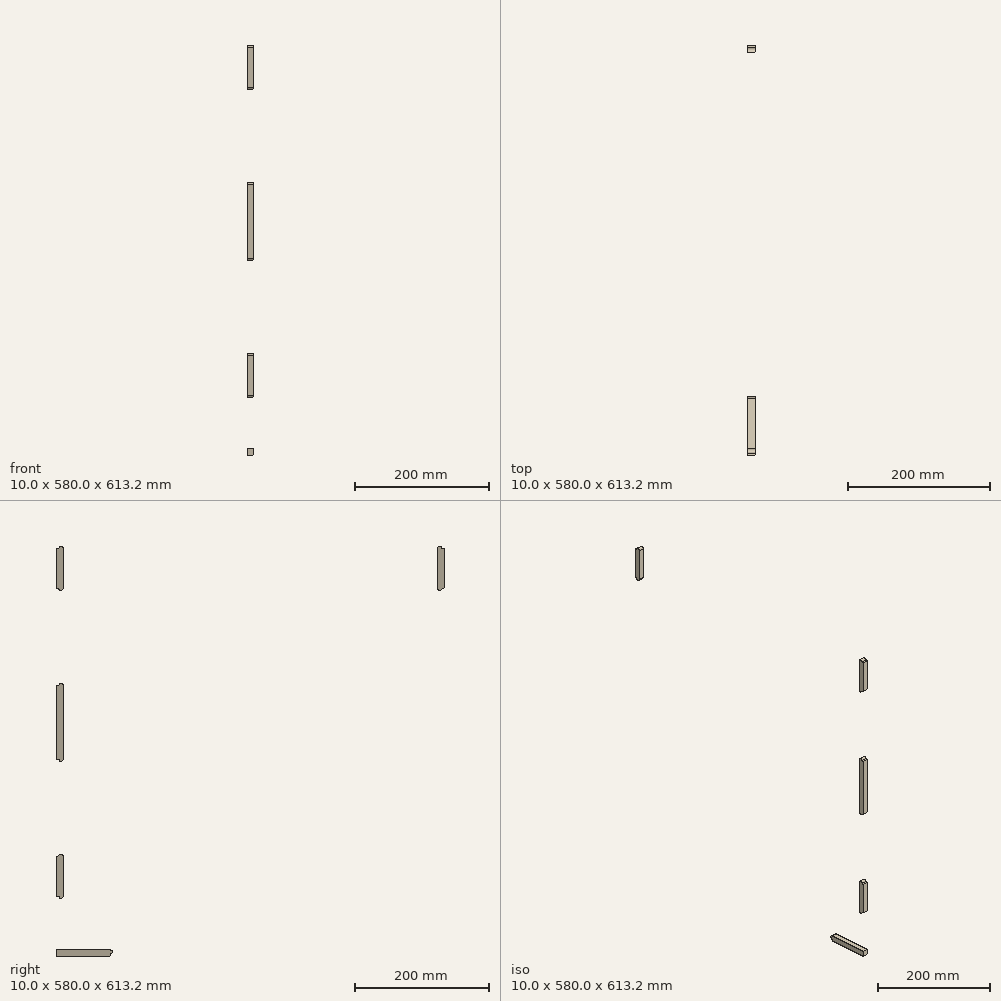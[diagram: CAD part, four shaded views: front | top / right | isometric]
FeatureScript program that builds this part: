
annotation { "Feature Type Name" : "Feature", "Feature Type Description" : "" }
export const myFeature = defineFeature(function(context is Context, id is Id, definition is map)
    precondition{}
    {
        {
            var Q0;
            Q0=qCreatedBy(makeId("Right.planeOp"),FACE);
            var sketch = newSketch(context, id + "F0", { "sketchPlane" : qUnion([Q0])});
            skLineSegment(sketch, "E0.bottom", {"start": v(290, -350) * mm, "end": v(-290, -350) * mm});
            skLineSegment(sketch, "E0.top", {"start": v(290, 350) * mm, "end": v(-290, 350) * mm});
            skLineSegment(sketch, "E0.left", {"start": v(290, -350) * mm, "end": v(290, 350) * mm});
            skLineSegment(sketch, "E0.right", {"start": v(-290, -350) * mm, "end": v(-290, 350) * mm});
            skPoint(sketch, "E0.middle", {"position": v(0, 0) * mm});
            skSolve(sketch);
        }
        {
            var Q0;
            Q0 = qSketchRegion(id + "F0", true);
            extrude(context, id + "F1", {"entities" : qUnion([Q0]), "depth" : 10 * mm, "offsetDistance" : 25 * mm});
        }
        {
            var Q0;
            Q0=makeQuery(id+"F1.opExtrude","CAP_FACE",FACE,{"disambiguationData":[OSD([sQuery(id+"F0.wireOp",EDGE,"E0.bottom"),sQuery(id+"F0.wireOp",EDGE,"E0.top"),sQuery(id+"F0.wireOp",EDGE,"E0.left"),sQuery(id+"F0.wireOp",EDGE,"E0.right")])],"isStart":false});
            var sketch = newSketch(context, id + "F2", { "sketchPlane" : qUnion([Q0])});
            skLineSegment(sketch, "E1", {"start": v(0, 350) * mm, "end": v(0, -350) * mm, "construction": true});
            skLineSegment(sketch, "E2", {"start": v(-281.72, 0) * mm, "end": v(290, 0) * mm, "construction": true});
            skLineSegment(sketch, "E3", {"start": v(150, -346.5) * mm, "end": v(150, -350) * mm});
            skLineSegment(sketch, "E4", {"start": v(210, -350) * mm, "end": v(210, -346.5) * mm});
            skLineSegment(sketch, "E5", {"start": v(210, -340) * mm, "end": v(290, -340) * mm});
            skLineSegment(sketch, "E6", {"start": v(290, -340) * mm, "end": v(290, -260) * mm});
            skLineSegment(sketch, "E7", {"start": v(290, -260) * mm, "end": v(286.5, -260) * mm});
            skLineSegment(sketch, "E8", {"start": v(280, -260) * mm, "end": v(280, -200) * mm});
            skLineSegment(sketch, "E9", {"start": v(286.5, -200) * mm, "end": v(290, -200) * mm});
            skLineSegment(sketch, "E10", {"start": v(290, -200) * mm, "end": v(290, -55) * mm});
            skLineSegment(sketch, "E11", {"start": v(290, -55) * mm, "end": v(286.5, -55) * mm});
            skLineSegment(sketch, "E12", {"start": v(280, -55) * mm, "end": v(280, 0) * mm});
            skArc(sketch, "E13", {"start": v(150, -346.5) * mm, "mid": v(153.25, -343.25) * mm, "end": v(150, -340) * mm});
            skArc(sketch, "E14", {"start": v(210, -340) * mm, "mid": v(206.75, -343.25) * mm, "end": v(210, -346.5) * mm});
            skArc(sketch, "E15", {"start": v(280, -55) * mm, "mid": v(283.25, -58.25) * mm, "end": v(286.5, -55) * mm});
            skArc(sketch, "E16", {"start": v(280, -260) * mm, "mid": v(283.25, -263.25) * mm, "end": v(286.5, -260) * mm});
            skArc(sketch, "E17", {"start": v(286.5, -200) * mm, "mid": v(283.25, -196.75) * mm, "end": v(280, -200) * mm});
            skLineSegment(sketch, "E18", {"start": v(150, -340) * mm, "end": v(55, -340) * mm});
            skLineSegment(sketch, "E19", {"start": v(210, -350) * mm, "end": v(150, -350) * mm});
            skLineSegment(sketch, "E20", {"start": v(55, -346.5) * mm, "end": v(55, -350) * mm});
            skLineSegment(sketch, "E21", {"start": v(55, -350) * mm, "end": v(0, -350) * mm});
            skArc(sketch, "E22", {"start": v(55, -340) * mm, "mid": v(51.75, -343.25) * mm, "end": v(55, -346.5) * mm});
            skLineSegment(sketch, "E23.MirrorCS", {"start": v(-150, -346.5) * mm, "end": v(-150, -350) * mm});
            skLineSegment(sketch, "E24.MirrorCS", {"start": v(-290, -260) * mm, "end": v(-286.5, -260) * mm});
            skArc(sketch, "E25.MirrorCS", {"start": v(-150, -346.5) * mm, "mid": v(-153.25, -343.25) * mm, "end": v(-150, -340) * mm});
            skLineSegment(sketch, "E26.MirrorCS", {"start": v(-290, -55) * mm, "end": v(-286.5, -55) * mm});
            skArc(sketch, "E27.MirrorCS", {"start": v(-280, -55) * mm, "mid": v(-283.25, -58.25) * mm, "end": v(-286.5, -55) * mm});
            skArc(sketch, "E28.MirrorCS", {"start": v(-280, -260) * mm, "mid": v(-283.25, -263.25) * mm, "end": v(-286.5, -260) * mm});
            skArc(sketch, "E29.MirrorCS", {"start": v(-55, -340) * mm, "mid": v(-51.75, -343.25) * mm, "end": v(-55, -346.5) * mm});
            skArc(sketch, "E30.MirrorCS", {"start": v(-210, -340) * mm, "mid": v(-206.75, -343.25) * mm, "end": v(-210, -346.5) * mm});
            skLineSegment(sketch, "E31.MirrorCS", {"start": v(-55, -346.5) * mm, "end": v(-55, -350) * mm});
            skArc(sketch, "E32.MirrorCS", {"start": v(-286.5, -200) * mm, "mid": v(-283.25, -196.75) * mm, "end": v(-280, -200) * mm});
            skLineSegment(sketch, "E33.MirrorCS", {"start": v(-286.5, -200) * mm, "end": v(-290, -200) * mm});
            skLineSegment(sketch, "E34.MirrorCS", {"start": v(-210, -350) * mm, "end": v(-210, -346.5) * mm});
            skLineSegment(sketch, "E35.MirrorCS", {"start": v(-55, -350) * mm, "end": v(0, -350) * mm});
            skLineSegment(sketch, "E36.MirrorCS", {"start": v(-210, -340) * mm, "end": v(-290, -340) * mm});
            skLineSegment(sketch, "E37.MirrorCS", {"start": v(-290, -340) * mm, "end": v(-290, -260) * mm});
            skLineSegment(sketch, "E38.MirrorCS", {"start": v(-210, -350) * mm, "end": v(-150, -350) * mm});
            skLineSegment(sketch, "E39.MirrorCS", {"start": v(-280, -55) * mm, "end": v(-280, 0) * mm});
            skLineSegment(sketch, "E40.MirrorCS", {"start": v(-280, -260) * mm, "end": v(-280, -200) * mm});
            skLineSegment(sketch, "E41.MirrorCS", {"start": v(-150, -340) * mm, "end": v(-55, -340) * mm});
            skLineSegment(sketch, "E42.MirrorCS", {"start": v(-290, -200) * mm, "end": v(-290, -55) * mm});
            skLineSegment(sketch, "E43.MirrorCS", {"start": v(281.72, 0) * mm, "end": v(-290, 0) * mm, "construction": true});
            skLineSegment(sketch, "E44.MirrorCS", {"start": v(55, 346.5) * mm, "end": v(55, 350) * mm});
            skArc(sketch, "E45.MirrorCS", {"start": v(55, 340) * mm, "mid": v(51.75, 343.25) * mm, "end": v(55, 346.5) * mm});
            skArc(sketch, "E46.MirrorCS", {"start": v(280, 260) * mm, "mid": v(283.25, 263.25) * mm, "end": v(286.5, 260) * mm});
            skArc(sketch, "E47.MirrorCS", {"start": v(-150, 346.5) * mm, "mid": v(-153.25, 343.25) * mm, "end": v(-150, 340) * mm});
            skArc(sketch, "E48.MirrorCS", {"start": v(280, 55) * mm, "mid": v(283.25, 58.25) * mm, "end": v(286.5, 55) * mm});
            skLineSegment(sketch, "E49.MirrorCS", {"start": v(210, 350) * mm, "end": v(210, 346.5) * mm});
            skLineSegment(sketch, "E50.MirrorCS", {"start": v(-290, 260) * mm, "end": v(-286.5, 260) * mm});
            skLineSegment(sketch, "E51.MirrorCS", {"start": v(290, 260) * mm, "end": v(286.5, 260) * mm});
            skArc(sketch, "E52.MirrorCS", {"start": v(210, 340) * mm, "mid": v(206.75, 343.25) * mm, "end": v(210, 346.5) * mm});
            skLineSegment(sketch, "E53.MirrorCS", {"start": v(286.5, 200) * mm, "end": v(290, 200) * mm});
            skArc(sketch, "E54.MirrorCS", {"start": v(-280, 260) * mm, "mid": v(-283.25, 263.25) * mm, "end": v(-286.5, 260) * mm});
            skLineSegment(sketch, "E55.MirrorCS", {"start": v(-150, 346.5) * mm, "end": v(-150, 350) * mm});
            skLineSegment(sketch, "E56.MirrorCS", {"start": v(290, 55) * mm, "end": v(286.5, 55) * mm});
            skArc(sketch, "E57.MirrorCS", {"start": v(-210, 340) * mm, "mid": v(-206.75, 343.25) * mm, "end": v(-210, 346.5) * mm});
            skLineSegment(sketch, "E58.MirrorCS", {"start": v(150, 346.5) * mm, "end": v(150, 350) * mm});
            skLineSegment(sketch, "E59.MirrorCS", {"start": v(-286.5, 200) * mm, "end": v(-290, 200) * mm});
            skArc(sketch, "E60.MirrorCS", {"start": v(286.5, 200) * mm, "mid": v(283.25, 196.75) * mm, "end": v(280, 200) * mm});
            skArc(sketch, "E61.MirrorCS", {"start": v(150, 346.5) * mm, "mid": v(153.25, 343.25) * mm, "end": v(150, 340) * mm});
            skLineSegment(sketch, "E62.MirrorCS", {"start": v(-210, 350) * mm, "end": v(-210, 346.5) * mm});
            skArc(sketch, "E63.MirrorCS", {"start": v(-286.5, 200) * mm, "mid": v(-283.25, 196.75) * mm, "end": v(-280, 200) * mm});
            skLineSegment(sketch, "E64.MirrorCS", {"start": v(-55, 346.5) * mm, "end": v(-55, 350) * mm});
            skArc(sketch, "E65.MirrorCS", {"start": v(-55, 340) * mm, "mid": v(-51.75, 343.25) * mm, "end": v(-55, 346.5) * mm});
            skLineSegment(sketch, "E66.MirrorCS", {"start": v(-290, 55) * mm, "end": v(-286.5, 55) * mm});
            skLineSegment(sketch, "E67.MirrorCS", {"start": v(55, 350) * mm, "end": v(0, 350) * mm});
            skArc(sketch, "E68.MirrorCS", {"start": v(-280, 55) * mm, "mid": v(-283.25, 58.25) * mm, "end": v(-286.5, 55) * mm});
            skLineSegment(sketch, "E69.MirrorCS", {"start": v(280, 260) * mm, "end": v(280, 200) * mm});
            skLineSegment(sketch, "E70.MirrorCS", {"start": v(150, 340) * mm, "end": v(55, 340) * mm});
            skLineSegment(sketch, "E71.MirrorCS", {"start": v(210, 340) * mm, "end": v(290, 340) * mm});
            skLineSegment(sketch, "E72.MirrorCS", {"start": v(290, 340) * mm, "end": v(290, 260) * mm});
            skLineSegment(sketch, "E73.MirrorCS", {"start": v(280, 55) * mm, "end": v(280, 0) * mm});
            skLineSegment(sketch, "E74.MirrorCS", {"start": v(-280, 55) * mm, "end": v(-280, 0) * mm});
            skLineSegment(sketch, "E75.MirrorCS", {"start": v(210, 350) * mm, "end": v(150, 350) * mm});
            skLineSegment(sketch, "E76.MirrorCS", {"start": v(-280, 260) * mm, "end": v(-280, 200) * mm});
            skLineSegment(sketch, "E77.MirrorCS", {"start": v(290, 200) * mm, "end": v(290, 55) * mm});
            skLineSegment(sketch, "E78.MirrorCS", {"start": v(-55, 350) * mm, "end": v(0, 350) * mm});
            skLineSegment(sketch, "E79.MirrorCS", {"start": v(-290, 200) * mm, "end": v(-290, 55) * mm});
            skLineSegment(sketch, "E80.MirrorCS", {"start": v(-150, 340) * mm, "end": v(-55, 340) * mm});
            skLineSegment(sketch, "E81.MirrorCS", {"start": v(-210, 350) * mm, "end": v(-150, 350) * mm});
            skLineSegment(sketch, "E82.MirrorCS", {"start": v(-210, 340) * mm, "end": v(-290, 340) * mm});
            skLineSegment(sketch, "E83.MirrorCS", {"start": v(-290, 340) * mm, "end": v(-290, 260) * mm});
            skSolve(sketch);
        }
        {
            var Q0;
            Q0=makeQuery(id+"F2.imprint","IMPRINT",FACE,{"disambiguationData":[TD([[makeQuery(id+"F2.imprint","IMPRINT",EDGE,{"derivedFrom":sQuery(id+"F2.wireOp",EDGE,"E30.MirrorCS")}),-1.0]])]});
            var Q1;
            {var subQ1=sQuery(id+"F2.wireOp",EDGE,"E23.MirrorCS");Q1=makeQuery(id+"F2.imprint","IMPRINT",FACE,{"disambiguationData":[TD([[makeQuery(id+"F2.imprint","IMPRINT",EDGE,{"derivedFrom":subQ1}),1.0]])]});}
            var Q2;
            {var subQ1=sQuery(id+"F2.wireOp",EDGE,"E3");Q2=makeQuery(id+"F2.imprint","IMPRINT",FACE,{"disambiguationData":[TD([[makeQuery(id+"F2.imprint","IMPRINT",EDGE,{"derivedFrom":subQ1}),-1.0]])]});}
            var Q3;
            {var subQ3=sQuery(id+"F2.wireOp",EDGE,"E4");Q3=makeQuery(id+"F2.imprint","IMPRINT",FACE,{"disambiguationData":[TD([[makeQuery(id+"F2.imprint","IMPRINT",EDGE,{"derivedFrom":subQ3}),-1.0]])]});}
            var Q4;
            {var subQ0=sQuery(id+"F2.wireOp",EDGE,"E7");Q4=makeQuery(id+"F2.imprint","IMPRINT",FACE,{"disambiguationData":[TD([[makeQuery(id+"F2.imprint","IMPRINT",EDGE,{"derivedFrom":subQ0}),-1.0]])]});}
            var Q5;
            {var subQ0=sQuery(id+"F2.wireOp",EDGE,"E11");Q5=makeQuery(id+"F2.imprint","IMPRINT",FACE,{"disambiguationData":[TD([[makeQuery(id+"F2.imprint","IMPRINT",EDGE,{"derivedFrom":subQ0}),-1.0]])]});}
            var Q6;
            Q6=makeQuery(id+"F2.imprint","IMPRINT",FACE,{"disambiguationData":[TD([[makeQuery(id+"F2.imprint","IMPRINT",EDGE,{"derivedFrom":sQuery(id+"F2.wireOp",EDGE,"E46.MirrorCS")}),-1.0]])]});
            var Q7;
            {var subQ3=sQuery(id+"F2.wireOp",EDGE,"E49.MirrorCS");Q7=makeQuery(id+"F2.imprint","IMPRINT",FACE,{"disambiguationData":[TD([[makeQuery(id+"F2.imprint","IMPRINT",EDGE,{"derivedFrom":subQ3}),1.0]])]});}
            var Q8;
            {var subQ1=sQuery(id+"F2.wireOp",EDGE,"E44.MirrorCS");Q8=makeQuery(id+"F2.imprint","IMPRINT",FACE,{"disambiguationData":[TD([[makeQuery(id+"F2.imprint","IMPRINT",EDGE,{"derivedFrom":subQ1}),-1.0]])]});}
            var Q9;
            Q9=makeQuery(id+"F2.imprint","IMPRINT",FACE,{"disambiguationData":[TD([[makeQuery(id+"F2.imprint","IMPRINT",EDGE,{"derivedFrom":sQuery(id+"F2.wireOp",EDGE,"E47.MirrorCS")}),1.0]])]});
            var Q10;
            Q10=makeQuery(id+"F2.imprint","IMPRINT",FACE,{"disambiguationData":[TD([[makeQuery(id+"F2.imprint","IMPRINT",EDGE,{"derivedFrom":sQuery(id+"F2.wireOp",EDGE,"E57.MirrorCS")}),1.0]])]});
            extrude(context, id + "F3", {"entities" : qUnion([Q0, Q1, Q2, Q3, Q4, Q5, Q6, Q7, Q8, Q9, Q10]), "operationType" : NewBodyOperationType.REMOVE, "endBound" : BoundingType.THROUGH_ALL, "oppositeDirection" : true, "depth" : 25 * mm, "offsetDistance" : 25 * mm});
        }
    });
